# Revit family: ASL_64_Series_al_door_100mm_head
name_source: partatom
category: Detail Items
revit_build: Autodesk Revit 2018 (Build: 20170223_1515(x64)
units: mm (PartAtom-declared; Revit-internal decimal feet)

## family parameters
Rotate with component = No
Section Shape = Not Defined
Shared = Yes

## types (4) — shared parameters
Manufacturer = Aluminate Solutions Limited
Technical Info = www.aluminate.nz

## per-type parameters (varying)
| type | Door Depth Parametric | Door Stop_ASL_547 | Flush Infil_ASL_648 | Glazing | Headsection_ASL_400 | Headsection_ASL_405S | Pocket Starter Cap_ASL_537 | Pocket Starter Cap_ASL_543 | Reven Seal | Top&Bottom Rail 100mm | Type Comments |
| Double Action ASL Door Suite 100mm | 22 mm  [stored 0.0721785 ft] | No | Yes | No | Yes | No | No | Yes | No | Yes | ASL 64 Series Head With Double Action ASL 100mm Door Suite |
| Single Action ASL Door Suite 100mm | 44 mm  [stored 0.144357 ft] | Yes | No | No | Yes | No | No | Yes | No | Yes | ASL 64 Series Head With Single Action ASL 100mm Door Suite |
| Single Action Raven Seal ASL Door Suite 100mm | 52 mm | No | No | No | No | Yes | Yes | No | Yes | Yes | ASL 64 Series Head With Single Action Raven Seal ASL 100mm Door Suite |
| Glazing | 44 mm  [stored 0.144357 ft] | No | No | Yes | Yes | No | No | Yes | No | No | ASL 64 Series Head With Glazing |

note: [stored X ft] marks values corroborated as IEEE doubles in the binary element streams (Revit-internal decimal feet)

## geometry (parser evidence)
native form markers: Sweep x13
no freeform markers — native parametric forms only
